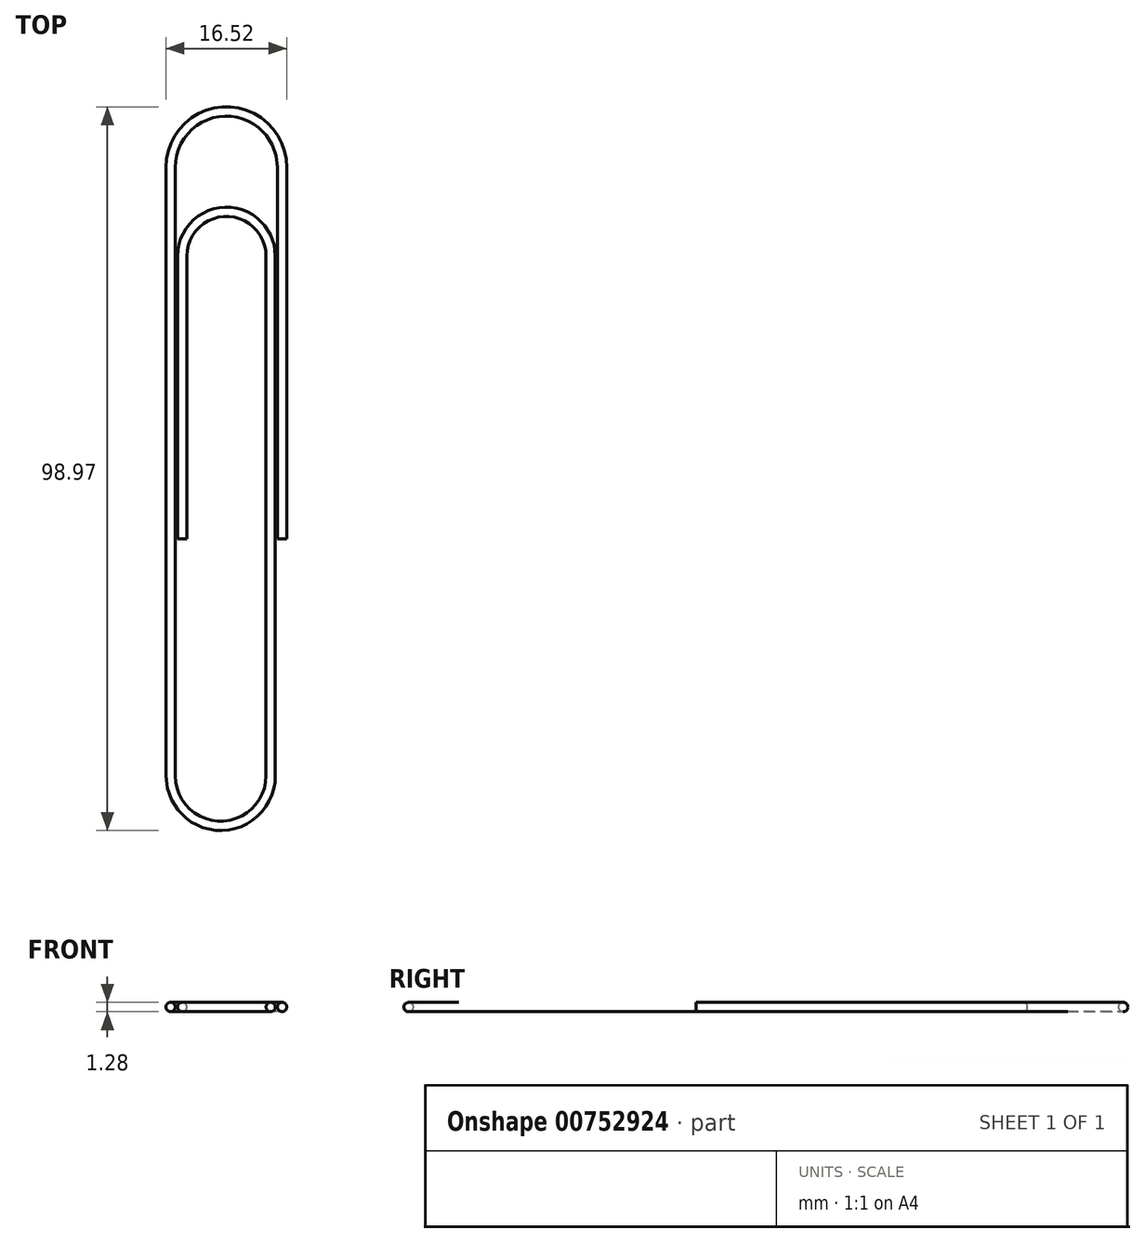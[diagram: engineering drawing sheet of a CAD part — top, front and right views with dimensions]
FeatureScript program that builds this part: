
annotation { "Feature Type Name" : "Feature", "Feature Type Description" : "" }
export const myFeature = defineFeature(function(context is Context, id is Id, definition is map)
    precondition{}
    {
        {
            var Q0;
            Q0=qCreatedBy(makeId("Front.planeOp"),FACE);
            var sketch = newSketch(context, id + "F0", { "sketchPlane" : qUnion([Q0])});
            skCircle(sketch, "E0", {"center": v(0, 0) * mm, "radius": 0.64 * mm});
            skSolve(sketch);
        }
        {
            var Q0;
            Q0=qCreatedBy(makeId("Top.planeOp"),FACE);
            var sketch = newSketch(context, id + "F1", { "sketchPlane" : qUnion([Q0])});
            skLineSegment(sketch, "E1", {"start": v(0, 0) * mm, "end": v(0, 50.8) * mm});
            skArc(sketch, "E2", {"start": v(0, 50.8) * mm, "mid": v(-7.62, 58.42) * mm, "end": v(-15.24, 50.8) * mm});
            skLineSegment(sketch, "E3", {"start": v(-15.24, 50.8) * mm, "end": v(-15.24, -32.43) * mm});
            skArc(sketch, "E4", {"start": v(-15.24, -32.43) * mm, "mid": v(-8.4, -39.27) * mm, "end": v(-1.56, -32.43) * mm});
            skLineSegment(sketch, "E5", {"start": v(-1.56, -32.43) * mm, "end": v(-1.56, 38.65) * mm});
            skArc(sketch, "E6", {"start": v(-1.56, 38.65) * mm, "mid": v(-7.6, 44.7) * mm, "end": v(-13.66, 38.65) * mm});
            skLineSegment(sketch, "E7", {"start": v(-13.66, 38.65) * mm, "end": v(-13.66, 0) * mm});
            skSolve(sketch);
        }
        {
            var Q0;
            Q0=makeQuery(id+"F0.imprint","IMPRINT",FACE,{"disambiguationData":[TD([[makeQuery(id+"F0.imprint","IMPRINT",EDGE,{"derivedFrom":sQuery(id+"F0.wireOp",EDGE,"E0")}),1.0]])]});
            var Q1;
            Q1=sQuery(id+"F1.wireOp",EDGE,"E1");
            var Q2;
            Q2=sQuery(id+"F1.wireOp",EDGE,"E2");
            var Q3;
            Q3=sQuery(id+"F1.wireOp",EDGE,"E3");
            var Q4;
            Q4=sQuery(id+"F1.wireOp",EDGE,"E4");
            var Q5;
            Q5=sQuery(id+"F1.wireOp",EDGE,"E5");
            var Q6;
            Q6=sQuery(id+"F1.wireOp",EDGE,"E6");
            var Q7;
            Q7=sQuery(id+"F1.wireOp",EDGE,"E7");
            sweep(context, id + "F2", {"profiles" : qUnion([Q0]), "path" : qUnion([Q1, Q2, Q3, Q4, Q5, Q6, Q7])});
        }
    });
